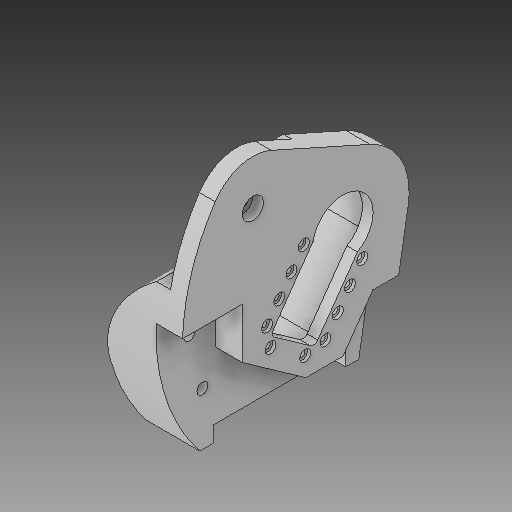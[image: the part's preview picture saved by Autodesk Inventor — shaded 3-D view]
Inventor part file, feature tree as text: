
AUTODESK INVENTOR PART (.ipt)
format: ipt  version: 2017 (Build 210142000, 142)  size: 311,808 bytes
history: native  units: mm
features: sketch x9, other x3
ambient origin geometry x8: Origin, YZ Plane, XZ Plane, XY Plane, X Axis, Y Axis, Z Axis, Center Point
bodies: Solid1 (feature_tree)
feature tree (12):
  other  "Arm - right shoulder v3.ipt"
  other  "Solid1::Arm - right shoulder v3.ipt"
  other  "TaggingFeature1"
  sketch  "Sketch1"  dims[d0=10.0mm]
  sketch  "Sketch2"
  sketch  "Sketch3"
  sketch  "Sketch4"
  sketch  "Sketch5"
  sketch  "Sketch6"
  sketch  "Sketch7"
  sketch  "Sketch8"
  sketch  "Sketch9"
